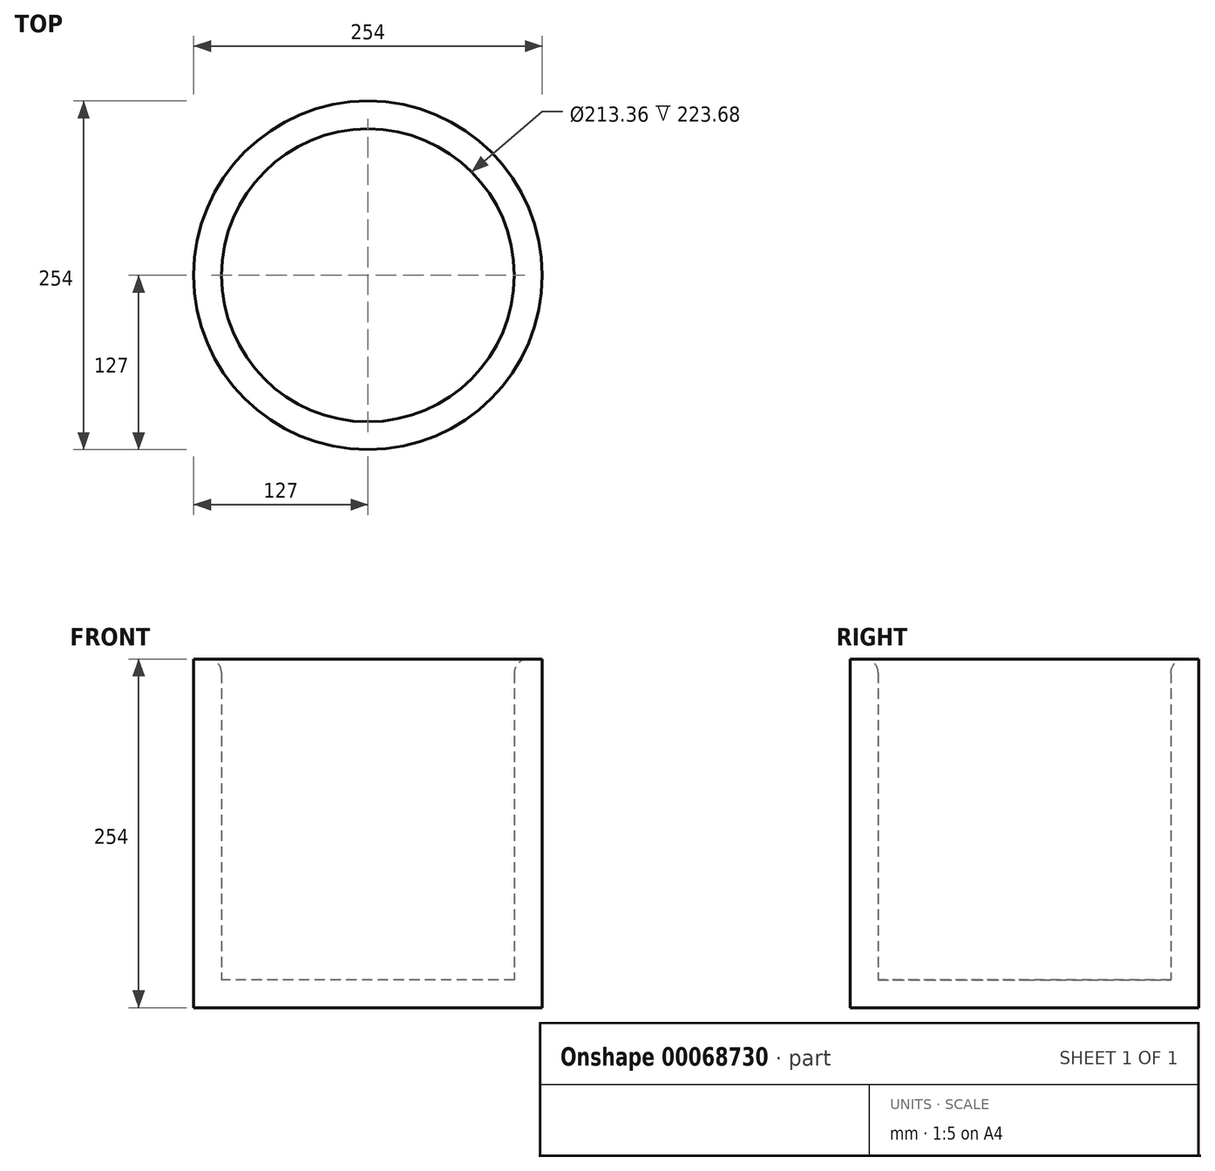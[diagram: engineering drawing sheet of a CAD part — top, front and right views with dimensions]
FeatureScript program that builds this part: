
annotation { "Feature Type Name" : "Feature", "Feature Type Description" : "" }
export const myFeature = defineFeature(function(context is Context, id is Id, definition is map)
    precondition{}
    {
        {
            var Q0;
            Q0=qCreatedBy(makeId("Top.planeOp"),FACE);
            var sketch = newSketch(context, id + "F3", { "sketchPlane" : qUnion([Q0])});
            skCircle(sketch, "E0", {"center": v(0, 0) * mm, "radius": 127 * mm});
            skSolve(sketch);
        }
        {
            var Q0;
            Q0 = qSketchRegion(id + "F3", true);
            extrude(context, id + "F0", {"entities" : qUnion([Q0]), "depth" : 254 * mm});
        }
        {
            var Q0;
            Q0=makeQuery(id+"F0.opExtrude","CAP_FACE",FACE,{"disambiguationData":[OSD([sQuery(id+"F3.wireOp",EDGE,"E0")])],"isStart":false});
            shell(context, id + "F1", {"entities" : qUnion([Q0]), "thickness" : 20.32 * mm});
        }
        {
            var Q0;
            {var subQ0=sQuery(id+"F3.wireOp",EDGE,"E0");Q0=makeQuery(id+"F1.opShell","OFFSET_EDGE",EDGE,{"disambiguationData":[OSD([subQ0]),TDD([makeQuery(id+"F0.opExtrude","CAP_EDGE",EDGE,{"disambiguationData":[OSD([subQ0])],"isStart":false})])]});}
            fillet(context, id + "F2", {"entities" : qUnion([Q0]), "radius" : 10 * mm, "tangentPropagation" : true, "allowEdgeOverflow" : false});
        }
    });
